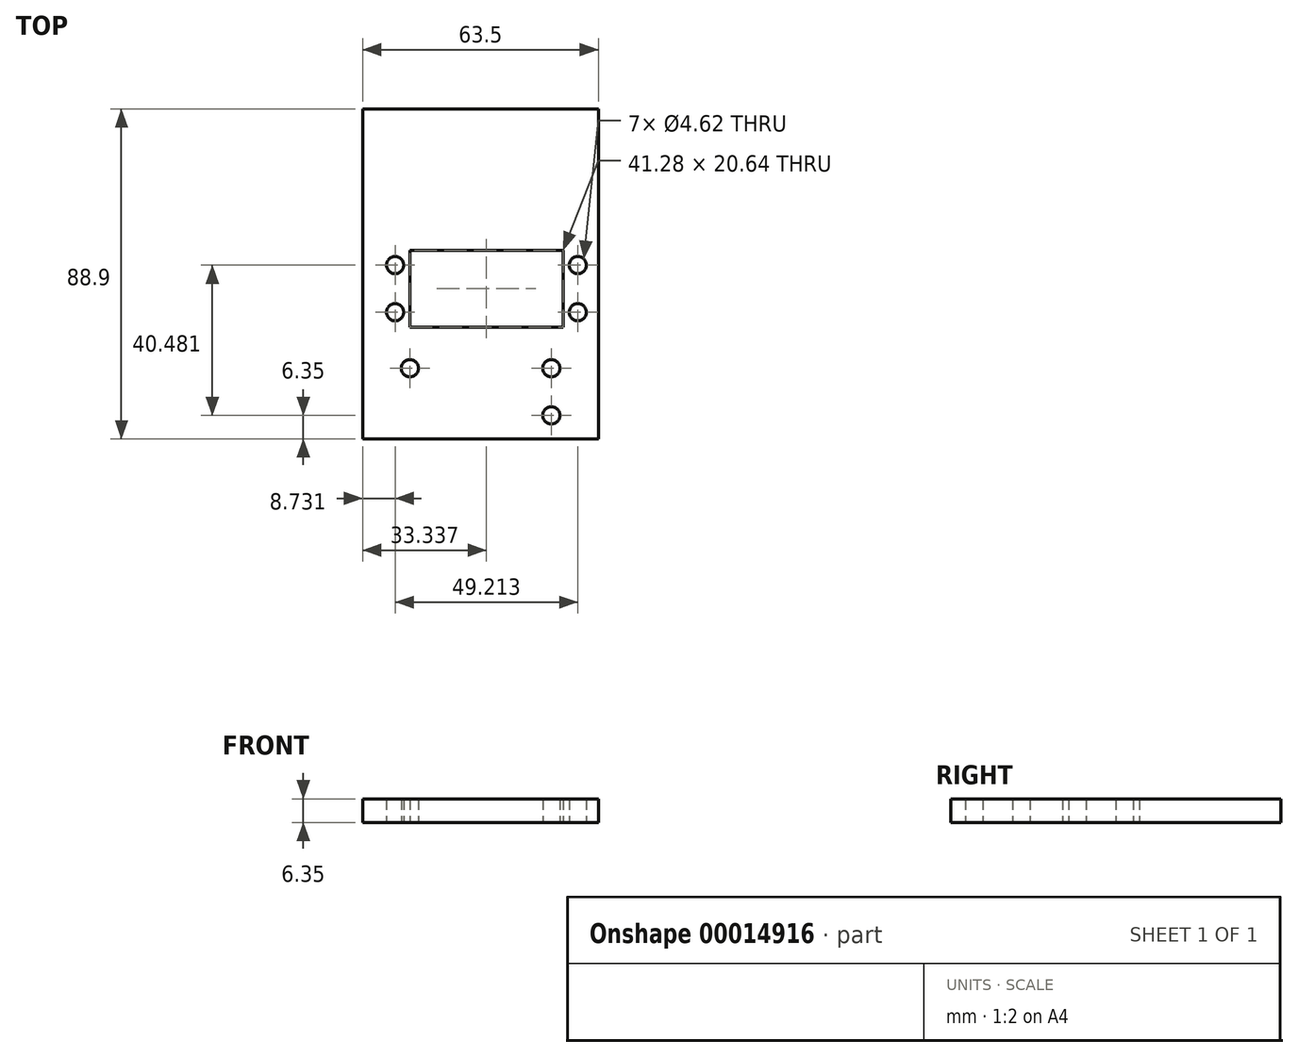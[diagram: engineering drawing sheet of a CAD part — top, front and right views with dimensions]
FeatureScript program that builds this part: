
annotation { "Feature Type Name" : "Feature", "Feature Type Description" : "" }
export const myFeature = defineFeature(function(context is Context, id is Id, definition is map)
    precondition{}
    {
        {
            var Q0;
            Q0=qCreatedBy(makeId("Top.planeOp"),FACE);
            var sketch = newSketch(context, id + "F0", { "sketchPlane" : qUnion([Q0])});
            skLineSegment(sketch, "E0.bottom", {"start": v(0, 88.9) * mm, "end": v(63.5, 88.9) * mm});
            skLineSegment(sketch, "E0.top", {"start": v(0, 0) * mm, "end": v(63.5, 0) * mm});
            skLineSegment(sketch, "E0.left", {"start": v(0, 88.9) * mm, "end": v(0, 0) * mm});
            skLineSegment(sketch, "E0.right", {"start": v(63.5, 88.9) * mm, "end": v(63.5, 0) * mm});
            skCircle(sketch, "E1", {"center": v(50.8, 6.35) * mm, "radius": 2.31 * mm});
            skCircle(sketch, "E2", {"center": v(12.7, 19.05) * mm, "radius": 2.31 * mm});
            skCircle(sketch, "E3", {"center": v(50.8, 19.05) * mm, "radius": 2.31 * mm});
            skLineSegment(sketch, "E4.bottom", {"start": v(12.7, 50.8) * mm, "end": v(53.98, 50.8) * mm});
            skLineSegment(sketch, "E4.top", {"start": v(12.7, 30.16) * mm, "end": v(53.98, 30.16) * mm});
            skLineSegment(sketch, "E4.left", {"start": v(12.7, 50.8) * mm, "end": v(12.7, 30.16) * mm});
            skLineSegment(sketch, "E4.right", {"start": v(53.98, 50.8) * mm, "end": v(53.98, 30.16) * mm});
            skCircle(sketch, "E5", {"center": v(8.73, 46.83) * mm, "radius": 2.31 * mm});
            skCircle(sketch, "E6", {"center": v(8.73, 34.13) * mm, "radius": 2.31 * mm});
            skCircle(sketch, "E7", {"center": v(57.94, 46.83) * mm, "radius": 2.31 * mm});
            skCircle(sketch, "E8", {"center": v(57.94, 34.13) * mm, "radius": 2.31 * mm});
            skPoint(sketch, "E9.third.point", {"position": v(33.34, 23.32) * mm});
            skPoint(sketch, "E9.third.point.positionSnap0", {"position": v(33.34, 30.16) * mm});
            skSolve(sketch);
        }
        {
            var Q0;
            Q0=makeQuery(id+"F0.imprint","IMPRINT",FACE,{"disambiguationData":[TD([[makeQuery(id+"F0.imprint","IMPRINT",EDGE,{"derivedFrom":sQuery(id+"F0.wireOp",EDGE,"E0.bottom")}),-1.0]])]});
            var Q1;
            {var subQ16=sQuery(id+"F0.wireOp",EDGE,"E0.top");Q1=makeQuery(id+"F0.imprint","IMPRINT",FACE,{"disambiguationData":[TD([[makeQuery(id+"F0.imprint","IMPRINT",EDGE,{"derivedFrom":subQ16}),1.0]])]});}
            var Q2;
            {var subQ1=sQuery(id+"F0.wireOp",EDGE,"1d1e5efa-8b46-4c2d-85fb-e1902345cae7");var subQ6=sQuery(id+"F0.wireOp",EDGE,"E0.bottom");var subQ7=makeQuery(id+"F0.imprint","INTERSECT",VERTEX,{"derivedFrom":[subQ6,subQ1]});Q2=makeQuery(id+"F0.imprint","IMPRINT",FACE,{"disambiguationData":[TD([[makeQuery(id+"F0.imprint","IMPRINT",EDGE,{"disambiguationData":[TD([[subQ7,-1.0]])],"derivedFrom":subQ1}),1.0]])]});}
            var Q3;
            {var subQ1=sQuery(id+"F0.wireOp",EDGE,"1d1e5efa-8b46-4c2d-85fb-e1902345cae7");var subQ6=sQuery(id+"F0.wireOp",EDGE,"E0.bottom");var subQ7=makeQuery(id+"F0.imprint","INTERSECT",VERTEX,{"derivedFrom":[subQ6,subQ1]});Q3=makeQuery(id+"F0.imprint","IMPRINT",FACE,{"disambiguationData":[TD([[makeQuery(id+"F0.imprint","IMPRINT",EDGE,{"disambiguationData":[TD([[subQ7,-1.0]])],"derivedFrom":subQ1}),-1.0]])]});}
            extrude(context, id + "F1", {"entities" : qUnion([Q0, Q1, Q2, Q3]), "depth" : 6.35 * mm});
        }
    });
